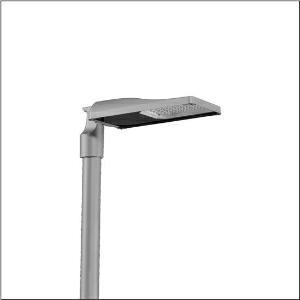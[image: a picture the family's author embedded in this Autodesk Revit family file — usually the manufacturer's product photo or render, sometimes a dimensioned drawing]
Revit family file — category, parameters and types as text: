
# Revit family: streetlight_sl_31_mini___st1_0a_5xh2d3ab08ja_f81c
name_source: partatom
category: Lighting Fixtures
units: mm (PartAtom-declared; Revit-internal decimal feet)

## family parameters
Cut with Voids When Loaded = No
Host = Face
Light Source = No
Part Type = Normal
Room Calculation Point = No
Round Connector Dimension = Use Diameter
Shared = No

## types (1)
- --- (1 x LED, 12140 lm, 81.1 W, 3000K)
    Apparent Load = 81 VA
    CIE Flux Codes = 40 73 97 100 100
    Color Rendering = 70
    Color Temperature = 3000K
    Default Elevation = 1800 mm
    Description = Streetlight SL 31 mini, mast luminaire, primary light control with lens, of PMMA, primary optical cover: cover, of toughened safety glass, transparent, light distribution: ST1.0a, light emission: direct distribution, primary light characteristic: asymmetric, installation type: post-top, side-entry, LED, High Power LED, rated luminous flux: 12.140lm, luminous efficacy: 150lm/W, light colour: 730, colour temperature: 3000K, control: presetting dimming linear, flexible luminous flux parameterisation, time-dependent luminous flux control, constant luminous flux control, power reduction, intelligent temperature release in ECG and LED module, overheat protection, with cable H07RN-F 3x 1.5mm², mains connection: 220..240V, AC, 50/60Hz, connection cable pre-assembled, cable length: 10,5m, start of lifetime: 81W, end of service life: 88W, reduction: 36W, luminaire housing, of diecast aluminium, powder-coated, Siteco® metallic grey (DB 702S), corrosivity category C5 high according to DIN EN ISO 12944, no sealing on luminaire upper side, inclination: -15°..+20° (post-top) | -20°..+20° (side-entry), adjustable in 5° steps, mast flange (76/60mm) included as standard, multi-level sealing system, sealing non-destructively replaceable, protection rating (complete): IP66, insulation class (complete): insulation class II (safety insulation), certification: CE, ENEC, ENEC+, VDE, UKCA, impact resistance: IK09, permissible operating ambient temperature for outdoor applications: -40..+50°C, standard-compliant lighting for roads and squares, packaging unit: 1 piece

Light Distribution: ST1.0a
    Height = 76 mm
    Lamp = 1 x LED
    Lamp Light Flux = 12140 lm
    Lamp Power = 81.1 W
    Lamp count = 1
    Length = 547 mm
    Luminous efficacy = 150 lm/W
    Manufacturer = Siteco
    ModVariant = No
    Model = 5XH2D3AB08JA
    Number of Poles = 1
    OnlyDefault = Yes
    Power Factor = 1
    Product Name = Streetlight SL 31 mini | ST1.0a
    Product group = mast luminaire | pylon top
    ProductGroupID = 6100
    Protection Class = Protection class II
    Protection Degree = IP 66
    RLX_Detail_Level = 1
    RLX_Emergency_Light_Flux = 0 lm
    RLX_Emergency_Type = 0
    RLX_Emergency_Type_DB = No
    RlxData = <blob elided: 40029 chars, md5=ff38112e>
    Socket = socket
    Standby Power = 0 W
    System Light Flux = 12140 lm
    System Power = 81 W
    Type Comments = factory setting: luminous flux: 100 % | dim-lin: 254 | 860 mA
    Type Image = l_1300326.jpg
    URL = http://relux.com
    VarID = @adj_008615
    Voltage = 0 V
    Weight = 0.00 kg
    Width = 265 mm

## geometry (parser evidence)
native form markers: Blend x4, Sweep x10
no freeform markers — native parametric forms only
